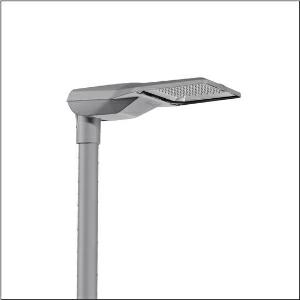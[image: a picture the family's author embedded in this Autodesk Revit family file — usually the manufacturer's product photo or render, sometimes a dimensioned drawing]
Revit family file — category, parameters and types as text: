
# Revit family: streetlight_sl_21_midi___st0_8a_5xe7c33a08lb_b9a8
name_source: partatom
category: Lighting Fixtures
units: mm (PartAtom-declared; Revit-internal decimal feet)

## family parameters
Cut with Voids When Loaded = No
Host = Face
Light Source = No
Part Type = Normal
Room Calculation Point = No
Round Connector Dimension = Use Diameter
Shared = No

## types (1)
- --- (1 x LED, 14340 lm, 98.3 W, 3000K)
    Apparent Load = 98 VA
    CIE Flux Codes = 38 75 97 100 100
    Color Rendering = 70
    Color Temperature = 3000K
    Default Elevation = 1800 mm
    Description = Streetlight SL 21 midi, mast luminaire, primary light control with lens, of PMMA, primary optical cover: cover, of toughened safety glass, transparent, light distribution: ST0.8a, light emission: direct distribution, primary light characteristic: asymmetric, installation type: post-top, side-entry, LED, 3G 1.5mm², High Power LED, rated luminous flux: 14.340lm, luminous efficacy: 146lm/W, light colour: 730, colour temperature: 3000K, control: overheat protection, constant luminous flux control, time-dependent luminous flux control, flexible luminous flux parameterisation, mains connection: 220..240V, AC, 50/60Hz, connection cable pre-assembled, cable length: 10,5m, wiring characteristics: H07RN-F, start of lifetime: 98W, end of service life: 101W, reduction: 44W, luminaire housing, of diecast aluminium, powder-coated, Siteco® metallic grey (DB 702S), corrosivity category C5 mid according to DIN EN ISO 12944, please order mast flange separately, inclination adjustable: 0°, 5°, 10°, 15°, sealing non-destructively replaceable, multi-level sealing system, length: 644mm, width: 335mm, height: 110mm, mast flange for spigot size: 42mm (side-entry): 5XC10008XM4, 60/48mm (side-entry/post-top): 5XC10108XM2, 76/60mm (side-entry/post-top): 5XC10108XM1, protection rating (complete): IP66, insulation class (complete): insulation class II (safety insulation), certification: CE, ENEC, ENEC+, VDE, impact resistance: IK09, permissible operating ambient temperature for outdoor applications: -40..+50°C, standard-compliant lighting for roads and squares, packaging unit: 1 piece

Light Distribution: ST0.8a
    Height = 111 mm
    Lamp = 1 x LED
    Lamp Light Flux = 14340 lm
    Lamp Power = 98.3 W
    Lamp count = 1
    Length = 644 mm
    Luminous efficacy = 146 lm/W
    Manufacturer = Siteco
    ModVariant = No
    Model = 5XE7C33A08LB
    Number of Poles = 1
    OnlyDefault = Yes
    Power Factor = 1
    Product Name = Streetlight SL 21 midi | ST0.8a
    Product group = mast luminaire | pylon top
    ProductGroupID = 6100
    Protection Class = Protection class II
    Protection Degree = IP 66
    RLX_Detail_Level = 1
    RLX_Emergency_Light_Flux = 0 lm
    RLX_Emergency_Type = 0
    RLX_Emergency_Type_DB = No
    RlxData = <blob elided: 90609 chars, md5=6760e2ca>
    Socket = socket
    Standby Power = 0 W
    System Light Flux = 14340 lm
    System Power = 98 W
    Type Comments = factory setting: luminous flux: 100 % | Output Level: 100 % | 1020 mA
    Type Image = l_1004298.jpg
    URL = http://relux.com
    VarID = @adj_137513
    Voltage = 0 V
    Weight = 0.00 kg
    Width = 336 mm

## geometry (parser evidence)
native form markers: Blend x4, Sweep x10
no freeform markers — native parametric forms only
